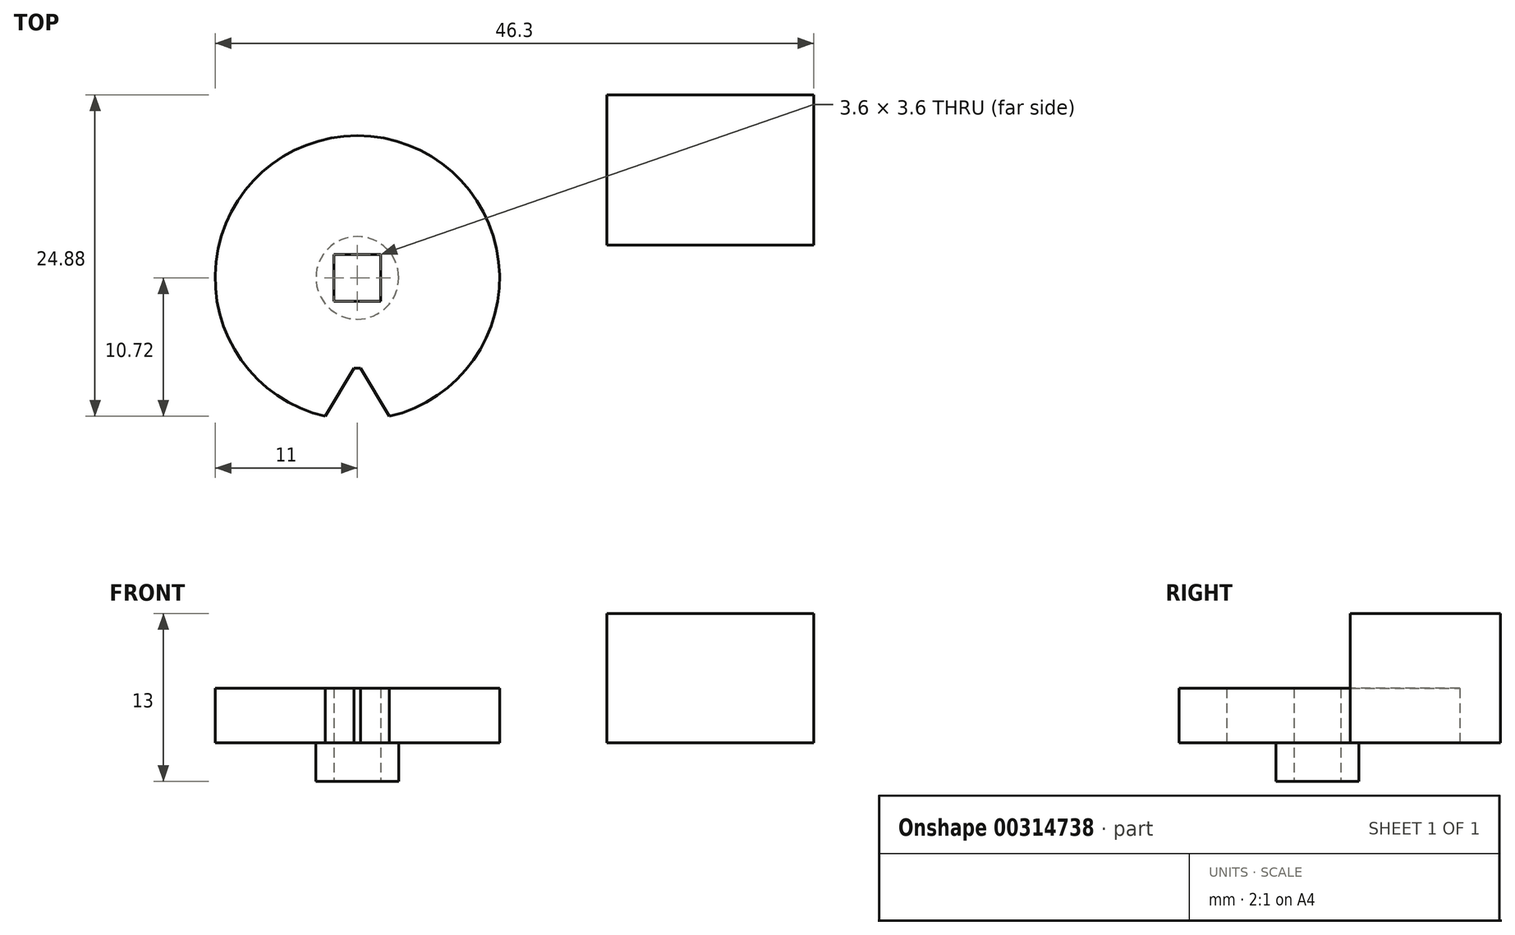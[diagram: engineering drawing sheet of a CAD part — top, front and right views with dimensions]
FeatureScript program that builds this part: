
annotation { "Feature Type Name" : "Feature", "Feature Type Description" : "" }
export const myFeature = defineFeature(function(context is Context, id is Id, definition is map)
    precondition{}
    {
        {
            var Q0;
            Q0=qCreatedBy(makeId("Top.planeOp"),FACE);
            var sketch = newSketch(context, id + "F0", { "sketchPlane" : qUnion([Q0])});
            skCircle(sketch, "E0", {"center": v(0, 0) * mm, "radius": 11 * mm});
            skSolve(sketch);
        }
        {
            var Q0;
            Q0=makeQuery(id+"F0.imprint","IMPRINT",FACE,{"disambiguationData":[TD([[makeQuery(id+"F0.imprint","IMPRINT",EDGE,{"derivedFrom":sQuery(id+"F0.wireOp",EDGE,"E0")}),1.0]])]});
            extrude(context, id + "F1", {"entities" : qUnion([Q0]), "depth" : 4.2 * mm});
        }
        {
            var Q0;
            Q0=makeQuery(id+"F1.opExtrude","CAP_FACE",FACE,{"disambiguationData":[OSD([sQuery(id+"F0.wireOp",EDGE,"E0")])],"isStart":false});
            var sketch = newSketch(context, id + "F2", { "sketchPlane" : qUnion([Q0])});
            skLineSegment(sketch, "E1", {"start": v(0, 0) * mm, "end": v(0, -11) * mm});
            skLineSegment(sketch, "E2", {"start": v(0, 0) * mm, "end": v(0.24, -7) * mm});
            skLineSegment(sketch, "E3", {"start": v(0, 0) * mm, "end": v(-0.24, -7) * mm});
            skLineSegment(sketch, "E4", {"start": v(0, 0) * mm, "end": v(-2.47, -10.72) * mm});
            skLineSegment(sketch, "E5", {"start": v(0, 0) * mm, "end": v(2.47, -10.72) * mm});
            skArc(sketch, "E6", {"start": v(0.24, -7) * mm, "mid": v(0, -7) * mm, "end": v(-0.24, -7) * mm});
            skArc(sketch, "E7", {"start": v(2.47, -10.72) * mm, "mid": v(0, -11) * mm, "end": v(-2.47, -10.72) * mm});
            skLineSegment(sketch, "E8", {"start": v(2.47, -10.72) * mm, "end": v(0.24, -7) * mm});
            skLineSegment(sketch, "E9", {"start": v(-2.47, -10.72) * mm, "end": v(-0.24, -7) * mm});
            skSolve(sketch);
        }
        {
            var Q0;
            {var subQ5=sQuery(id+"F2.wireOp",EDGE,"E8");Q0=makeQuery(id+"F2.imprint","IMPRINT",FACE,{"disambiguationData":[TD([[makeQuery(id+"F2.imprint","IMPRINT",EDGE,{"derivedFrom":subQ5}),1.0]])]});}
            var Q1;
            {var subQ5=sQuery(id+"F2.wireOp",EDGE,"E9");Q1=makeQuery(id+"F2.imprint","IMPRINT",FACE,{"disambiguationData":[TD([[makeQuery(id+"F2.imprint","IMPRINT",EDGE,{"derivedFrom":subQ5}),-1.0]])]});}
            extrude(context, id + "F3", {"entities" : qUnion([Q0, Q1]), "operationType" : NewBodyOperationType.REMOVE, "endBound" : BoundingType.THROUGH_ALL, "oppositeDirection" : true, "depth" : 25 * mm});
        }
        {
            var Q0;
            Q0=qCreatedBy(makeId("Front.planeOp"),FACE);
            var sketch = newSketch(context, id + "F4", { "sketchPlane" : qUnion([Q0])});
            skLineSegment(sketch, "E10", {"start": v(0, 0) * mm, "end": v(0, -12.05) * mm});
            skSolve(sketch);
        }
        {
            var Q0;
            Q0=makeQuery(id+"F1.opExtrude","CAP_FACE",FACE,{"disambiguationData":[OSD([sQuery(id+"F0.wireOp",EDGE,"E0")])],"isStart":true});
            var sketch = newSketch(context, id + "F5", { "sketchPlane" : qUnion([Q0])});
            skCircle(sketch, "E11", {"center": v(0, 0) * mm, "radius": 3.2 * mm});
            skSolve(sketch);
        }
        {
            var Q0;
            Q0 = qSketchRegion(id + "F5", true);
            extrude(context, id + "F6", {"entities" : qUnion([Q0]), "operationType" : NewBodyOperationType.ADD, "depth" : 3 * mm});
        }
        {
            var Q0;
            Q0=makeQuery(id+"F6.opExtrude","CAP_FACE",FACE,{"disambiguationData":[OSD([sQuery(id+"F5.wireOp",EDGE,"E11")])],"isStart":false});
            var sketch = newSketch(context, id + "F7", { "sketchPlane" : qUnion([Q0])});
            skLineSegment(sketch, "E12.bottom", {"start": v(-1.8, 1.8) * mm, "end": v(1.8, 1.8) * mm});
            skLineSegment(sketch, "E12.top", {"start": v(-1.8, -1.8) * mm, "end": v(1.8, -1.8) * mm});
            skLineSegment(sketch, "E12.left", {"start": v(-1.8, 1.8) * mm, "end": v(-1.8, -1.8) * mm});
            skLineSegment(sketch, "E12.right", {"start": v(1.8, 1.8) * mm, "end": v(1.8, -1.8) * mm});
            skPoint(sketch, "E12.middle", {"position": v(0, 0) * mm});
            skSolve(sketch);
        }
        {
            var Q0;
            Q0 = qSketchRegion(id + "F7", true);
            extrude(context, id + "F8", {"entities" : qUnion([Q0]), "operationType" : NewBodyOperationType.REMOVE, "endBound" : BoundingType.THROUGH_ALL, "oppositeDirection" : true, "depth" : 20 * mm});
        }
        {
            var Q0;
            Q0=qCreatedBy(makeId("Top.planeOp"),FACE);
            var sketch = newSketch(context, id + "F9", { "sketchPlane" : qUnion([Q0])});
            skLineSegment(sketch, "E13.bottom", {"start": v(35.3, 14.16) * mm, "end": v(19.3, 14.16) * mm});
            skLineSegment(sketch, "E13.top", {"start": v(35.3, 2.54) * mm, "end": v(19.3, 2.54) * mm});
            skLineSegment(sketch, "E13.left", {"start": v(35.3, 14.16) * mm, "end": v(35.3, 2.54) * mm});
            skLineSegment(sketch, "E13.right", {"start": v(19.3, 14.16) * mm, "end": v(19.3, 2.54) * mm});
            skPoint(sketch, "E13.middle", {"position": v(27.3, 8.35) * mm});
            skSolve(sketch);
        }
        {
            var Q0;
            Q0 = qSketchRegion(id + "F9", true);
            extrude(context, id + "F10", {"entities" : qUnion([Q0]), "depth" : 10 * mm});
        }
    });
